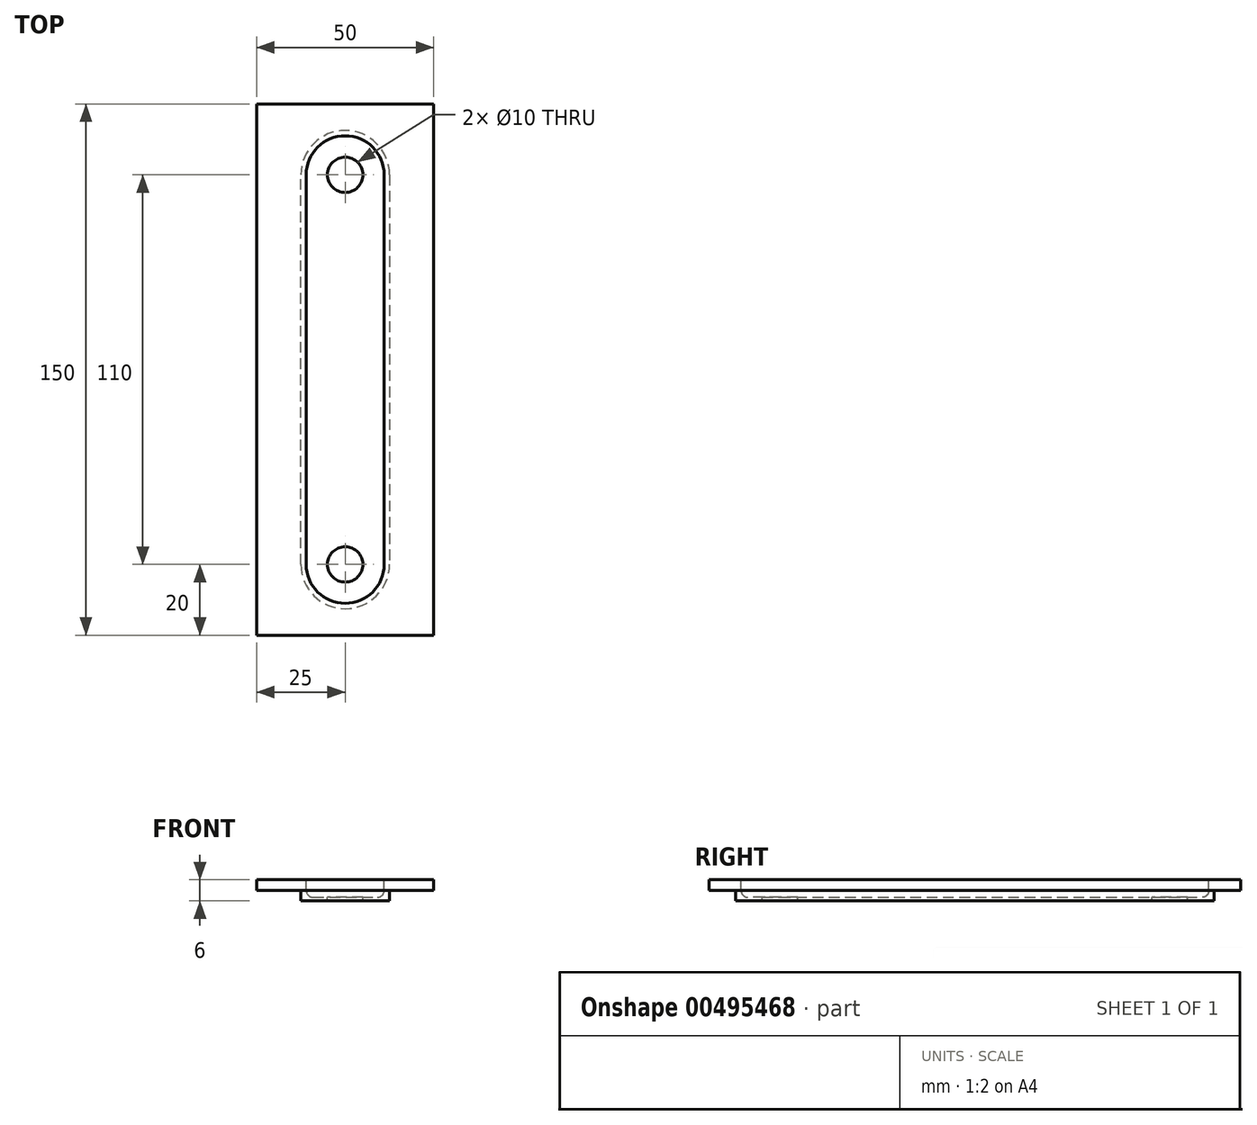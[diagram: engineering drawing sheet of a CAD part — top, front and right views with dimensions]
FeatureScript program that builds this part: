
annotation { "Feature Type Name" : "Feature", "Feature Type Description" : "" }
export const myFeature = defineFeature(function(context is Context, id is Id, definition is map)
    precondition{}
    {
        {
            var Q0;
            Q0=qCreatedBy(makeId("Top.planeOp"),FACE);
            var sketch = newSketch(context, id + "F0", { "sketchPlane" : qUnion([Q0])});
            skLineSegment(sketch, "E0.bottom", {"start": v(0, 0) * mm, "end": v(50, 0) * mm});
            skLineSegment(sketch, "E0.top", {"start": v(0, 150) * mm, "end": v(50, 150) * mm});
            skLineSegment(sketch, "E0.left", {"start": v(0, 0) * mm, "end": v(0, 150) * mm});
            skLineSegment(sketch, "E0.right", {"start": v(50, 0) * mm, "end": v(50, 150) * mm});
            skSolve(sketch);
        }
        {
            var Q0;
            Q0=qSketchRegion(id+"F0",true);
            extrude(context, id + "F1", {"entities" : qUnion([Q0]), "depth" : 3 * mm});
        }
        {
            var Q0;
            Q0=makeQuery(id+"F1.opExtrude","CAP_FACE",FACE,{"disambiguationData":[OSD([sQuery(id+"F0.wireOp",EDGE,"E0.bottom"),sQuery(id+"F0.wireOp",EDGE,"E0.top"),sQuery(id+"F0.wireOp",EDGE,"E0.left"),sQuery(id+"F0.wireOp",EDGE,"E0.right")])],"isStart":false});
            var sketch = newSketch(context, id + "F2", { "sketchPlane" : qUnion([Q0])});
            skCircle(sketch, "E1", {"center": v(25, 20) * mm, "radius": 5 * mm});
            skCircle(sketch, "E2", {"center": v(25, 130) * mm, "radius": 5 * mm});
            skSolve(sketch);
        }
        {
            var Q0;
            Q0=makeQuery(id+"F1.opExtrude","CAP_FACE",FACE,{"disambiguationData":[OSD([sQuery(id+"F0.wireOp",EDGE,"E0.bottom"),sQuery(id+"F0.wireOp",EDGE,"E0.top"),sQuery(id+"F0.wireOp",EDGE,"E0.left"),sQuery(id+"F0.wireOp",EDGE,"E0.right")])],"isStart":false});
            var sketch = newSketch(context, id + "F3", { "sketchPlane" : qUnion([Q0])});
            skArc(sketch, "E3", {"start": v(37.5, 130) * mm, "mid": v(25, 142.5) * mm, "end": v(12.5, 130) * mm});
            skArc(sketch, "E4", {"start": v(12.5, 20) * mm, "mid": v(25, 7.5) * mm, "end": v(37.5, 20) * mm});
            skLineSegment(sketch, "E5", {"start": v(37.5, 130) * mm, "end": v(37.5, 20) * mm});
            skLineSegment(sketch, "E6", {"start": v(12.5, 20) * mm, "end": v(12.5, 130) * mm});
            skArc(sketch, "E7", {"start": v(14, 20) * mm, "mid": v(25, 9) * mm, "end": v(36, 20) * mm});
            skArc(sketch, "E8", {"start": v(36, 130) * mm, "mid": v(25, 141) * mm, "end": v(14, 130) * mm});
            skLineSegment(sketch, "E9", {"start": v(14, 20) * mm, "end": v(14, 130) * mm});
            skLineSegment(sketch, "E10", {"start": v(36, 130) * mm, "end": v(36, 20) * mm});
            skSolve(sketch);
        }
        {
            var Q0;
            Q0=makeQuery(id+"F3.imprint","IMPRINT",FACE,{"disambiguationData":[TD([[makeQuery(id+"F3.imprint","IMPRINT",EDGE,{"derivedFrom":sQuery(id+"F3.wireOp",EDGE,"E3")}),1.0]])]});
            var Q1;
            Q1=makeQuery(id+"F3.imprint","IMPRINT",FACE,{"disambiguationData":[TD([[makeQuery(id+"F3.imprint","IMPRINT",EDGE,{"derivedFrom":sQuery(id+"F3.wireOp",EDGE,"E7")}),1.0]])]});
            extrude(context, id + "F4", {"entities" : qUnion([Q0, Q1]), "operationType" : NewBodyOperationType.ADD, "oppositeDirection" : true, "depth" : 6 * mm});
        }
        {
            var Q0;
            Q0=qSketchRegion(id+"F2",true);
            extrude(context, id + "F5", {"entities" : qUnion([Q0]), "operationType" : NewBodyOperationType.REMOVE, "endBound" : BoundingType.THROUGH_ALL, "oppositeDirection" : true, "depth" : 25 * mm});
        }
        {
            var Q0;
            Q0=makeQuery(id+"F3.imprint","IMPRINT",FACE,{"disambiguationData":[TD([[makeQuery(id+"F3.imprint","IMPRINT",EDGE,{"derivedFrom":sQuery(id+"F3.wireOp",EDGE,"E7")}),1.0]])]});
            extrude(context, id + "F6", {"entities" : qUnion([Q0]), "operationType" : NewBodyOperationType.REMOVE, "oppositeDirection" : true, "depth" : 5 * mm});
        }
        {
            var Q0;
            Q0=makeQuery(id+"F6.boolean.opBoolean","COPY",EDGE,{"derivedFrom":makeQuery(id+"F6.opExtrude","CAP_EDGE",EDGE,{"disambiguationData":[OSD([sQuery(id+"F3.wireOp",EDGE,"E9")])],"isStart":true})});
            var Q1;
            Q1=makeQuery(id+"F6.boolean.opBoolean","COPY",EDGE,{"derivedFrom":makeQuery(id+"F6.opExtrude","CAP_EDGE",EDGE,{"disambiguationData":[OSD([sQuery(id+"F3.wireOp",EDGE,"E9")])],"isStart":false})});
            fillet(context, id + "F7", {"entities" : qUnion([Q0, Q1]), "radius" : 2 * mm, "tangentPropagation" : true, "allowEdgeOverflow" : false});
        }
    });
